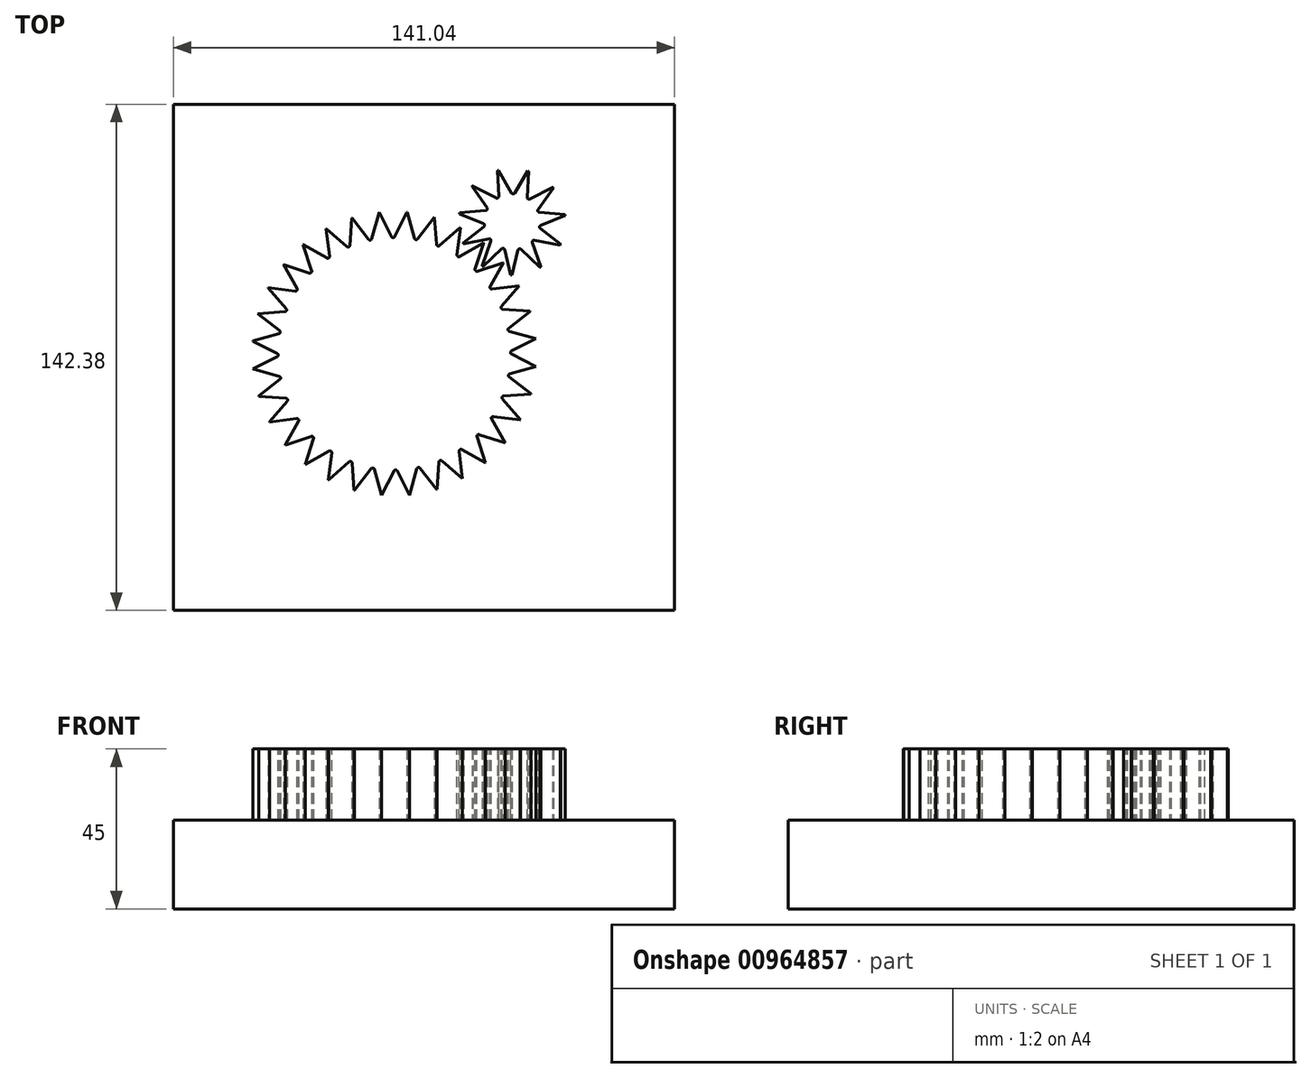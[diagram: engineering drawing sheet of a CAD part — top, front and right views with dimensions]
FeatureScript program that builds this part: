
annotation { "Feature Type Name" : "Feature", "Feature Type Description" : "" }
export const myFeature = defineFeature(function(context is Context, id is Id, definition is map)
    precondition{}
    {
        {
            var Q0;
            Q0=qCreatedBy(makeId("Top.planeOp"),FACE);
            var sketch = newSketch(context, id + "F0", { "sketchPlane" : qUnion([Q0])});
            skCircle(sketch, "E0", {"center": v(0, 0) * mm, "radius": 40 * mm});
            skPoint(sketch, "E1.right.start.orphan", {"position": v(-10, 5) * mm});
            skPoint(sketch, "E1.top.end.orphan", {"position": v(-10, -5) * mm});
            skPoint(sketch, "E1.left.end.orphan", {"position": v(10, -5) * mm});
            skPoint(sketch, "E1.left.start.orphan", {"position": v(10, 5) * mm});
            skSolve(sketch);
        }
        {
            var Q0;
            Q0=makeQuery(id+"F0.imprint","IMPRINT",FACE,{"disambiguationData":[TD([[makeQuery(id+"F0.imprint","IMPRINT",EDGE,{"derivedFrom":sQuery(id+"F0.wireOp",EDGE,"E0")}),1.0]])]});
            extrude(context, id + "F1", {"entities" : qUnion([Q0]), "depth" : 20 * mm, "offsetDistance" : 25 * mm});
        }
        {
            var Q0;
            Q0=makeQuery(id+"F1.opExtrude","CAP_FACE",FACE,{"disambiguationData":[OSD([sQuery(id+"F0.wireOp",EDGE,"E0"),sQuery(id+"F0.wireOp",EDGE,"E1.bottom"),sQuery(id+"F0.wireOp",EDGE,"E1.top"),sQuery(id+"F0.wireOp",EDGE,"E1.left"),sQuery(id+"F0.wireOp",EDGE,"E1.right")])],"isStart":false});
            var sketch = newSketch(context, id + "F2", { "sketchPlane" : qUnion([Q0])});
            skLineSegment(sketch, "E2", {"start": v(-4.86, 41) * mm, "end": v(4.14, 41) * mm});
            skLineSegment(sketch, "E3", {"start": v(4.14, 41) * mm, "end": v(0.08, 32.96) * mm});
            skLineSegment(sketch, "E4", {"start": v(-0.8, 32.96) * mm, "end": v(-4.86, 41) * mm});
            skPoint(sketch, "E5.visualSharp", {"position": v(-0.36, 32.08) * mm});
            skArc(sketch, "E5.filletArc", {"start": v(-0.8, 32.96) * mm, "mid": v(-0.36, 32.69) * mm, "end": v(0.08, 32.96) * mm});
            skSolve(sketch);
        }
        {
            var Q0;
            {var subQ0=sQuery(id+"F2.wireOp",EDGE,"E4");var subQ1=sQuery(id+"F2.wireOp",EDGE,"E3");var subQ2=makeQuery(id+"F2.imprint","INTERSECT",VERTEX,{"derivedFrom":[subQ1,subQ0]});Q0=makeQuery(id+"F2.imprint","IMPRINT",FACE,{"disambiguationData":[TD([[makeQuery(id+"F2.imprint","IMPRINT",EDGE,{"disambiguationData":[TD([[subQ2,1.0]])],"derivedFrom":subQ1}),-1.0]])]});}
            extrude(context, id + "F3", {"entities" : qUnion([Q0]), "operationType" : NewBodyOperationType.REMOVE, "oppositeDirection" : true, "depth" : 25 * mm, "offsetDistance" : 25 * mm});
        }
        {
            var Q0;
            Q0=makeQuery(id+"F3.boolean.opBoolean","COPY",FACE,{"derivedFrom":makeQuery(id+"F3.opExtrude","SWEPT_FACE",FACE,{"disambiguationData":[OSD([sQuery(id+"F2.wireOp",EDGE,"E4")])]})});
            var Q1;
            Q1=makeQuery(id+"F3.boolean.opBoolean","COPY",FACE,{"derivedFrom":makeQuery(id+"F3.opExtrude","SWEPT_FACE",FACE,{"disambiguationData":[OSD([sQuery(id+"F2.wireOp",EDGE,"E3")])]})});
            var Q2;
            Q2=makeQuery(id+"F3.boolean.opBoolean","COPY",FACE,{"derivedFrom":makeQuery(id+"F3.opExtrude","SWEPT_FACE",FACE,{"disambiguationData":[OSD([sQuery(id+"F2.wireOp",EDGE,"E5.filletArc")])]})});
            var Q3;
            Q3=makeQuery(id+"F1.opExtrude","SWEPT_FACE",FACE,{"disambiguationData":[OSD([sQuery(id+"F0.wireOp",EDGE,"E0")])]});
            circularPattern(context, id + "F4", {"patternType" : PatternType.FACE, "faces" : qUnion([Q0, Q1, Q2]), "axis" : qUnion([Q3]), "angle" : 360 * degree, "instanceCount" : 64, "equalSpace" : true});
        }
        {
            var Q0;
            Q0=qCreatedBy(makeId("Top.planeOp"),FACE);
            var sketch = newSketch(context, id + "F5", { "sketchPlane" : qUnion([Q0])});
            skCircle(sketch, "E6", {"center": v(40.75, 48.43) * mm, "radius": 15 * mm});
            skPoint(sketch, "E7.right.end.orphan", {"position": v(38.25, 47.43) * mm});
            skPoint(sketch, "E7.bottom.end.orphan", {"position": v(38.25, 49.43) * mm});
            skPoint(sketch, "E7.left.end.orphan", {"position": v(43.25, 47.43) * mm});
            skPoint(sketch, "E7.left.start.orphan", {"position": v(43.25, 49.43) * mm});
            skSolve(sketch);
        }
        {
            var Q0;
            Q0=makeQuery(id+"F5.imprint","IMPRINT",FACE,{"disambiguationData":[TD([[makeQuery(id+"F5.imprint","IMPRINT",EDGE,{"derivedFrom":sQuery(id+"F5.wireOp",EDGE,"E6")}),1.0]])]});
            extrude(context, id + "F6", {"entities" : qUnion([Q0]), "operationType" : NewBodyOperationType.ADD, "depth" : 20 * mm, "offsetDistance" : 25 * mm});
        }
        {
            var Q0;
            Q0=makeQuery(id+"F6.opExtrude","CAP_FACE",FACE,{"disambiguationData":[OSD([sQuery(id+"F5.wireOp",EDGE,"E6"),sQuery(id+"F5.wireOp",EDGE,"E7.bottom"),sQuery(id+"F5.wireOp",EDGE,"E7.top"),sQuery(id+"F5.wireOp",EDGE,"E7.left"),sQuery(id+"F5.wireOp",EDGE,"E7.right")])],"isStart":false});
            var sketch = newSketch(context, id + "F7", { "sketchPlane" : qUnion([Q0])});
            skLineSegment(sketch, "E8", {"start": v(36.02, 64.43) * mm, "end": v(46.02, 64.43) * mm});
            skLineSegment(sketch, "E9", {"start": v(46.02, 64.43) * mm, "end": v(41.45, 56.52) * mm});
            skLineSegment(sketch, "E10", {"start": v(40.59, 56.52) * mm, "end": v(36.02, 64.43) * mm});
            skPoint(sketch, "E11.visualSharp", {"position": v(41.02, 55.77) * mm});
            skArc(sketch, "E11.filletArc", {"start": v(40.59, 56.52) * mm, "mid": v(41.02, 56.27) * mm, "end": v(41.45, 56.52) * mm});
            skSolve(sketch);
        }
        {
            var Q0;
            {var subQ0=sQuery(id+"F7.wireOp",EDGE,"E10");var subQ1=sQuery(id+"F7.wireOp",EDGE,"E9");var subQ2=makeQuery(id+"F7.imprint","INTERSECT",VERTEX,{"derivedFrom":[subQ1,subQ0]});Q0=makeQuery(id+"F7.imprint","IMPRINT",FACE,{"disambiguationData":[TD([[makeQuery(id+"F7.imprint","IMPRINT",EDGE,{"disambiguationData":[TD([[subQ2,1.0]])],"derivedFrom":subQ1}),-1.0]])]});}
            extrude(context, id + "F8", {"entities" : qUnion([Q0]), "operationType" : NewBodyOperationType.REMOVE, "oppositeDirection" : true, "depth" : 20 * mm, "offsetDistance" : 25 * mm});
        }
        {
            var Q0;
            Q0=makeQuery(id+"F8.boolean.opBoolean","COPY",FACE,{"derivedFrom":makeQuery(id+"F8.opExtrude","SWEPT_FACE",FACE,{"disambiguationData":[OSD([sQuery(id+"F7.wireOp",EDGE,"E10")])]})});
            var Q1;
            Q1=makeQuery(id+"F8.boolean.opBoolean","COPY",FACE,{"derivedFrom":makeQuery(id+"F8.opExtrude","SWEPT_FACE",FACE,{"disambiguationData":[OSD([sQuery(id+"F7.wireOp",EDGE,"E9")])]})});
            var Q2;
            Q2=makeQuery(id+"F8.boolean.opBoolean","COPY",FACE,{"derivedFrom":makeQuery(id+"F8.opExtrude","SWEPT_FACE",FACE,{"disambiguationData":[OSD([sQuery(id+"F7.wireOp",EDGE,"E11.filletArc")])]})});
            var Q3;
            Q3=makeQuery(id+"F6.opExtrude","SWEPT_FACE",FACE,{"disambiguationData":[OSD([sQuery(id+"F5.wireOp",EDGE,"E6")])]});
            circularPattern(context, id + "F9", {"patternType" : PatternType.FACE, "faces" : qUnion([Q0, Q1, Q2]), "axis" : qUnion([Q3]), "angle" : 360 * degree, "instanceCount" : 22, "equalSpace" : true});
        }
        {
            var Q0;
            Q0=qCreatedBy(makeId("Top.planeOp"),FACE);
            var sketch = newSketch(context, id + "F10", { "sketchPlane" : qUnion([Q0])});
            skLineSegment(sketch, "E12.bottom", {"start": v(-62.2, 70.17) * mm, "end": v(78.84, 70.17) * mm});
            skLineSegment(sketch, "E12.top", {"start": v(-62.2, -72.2) * mm, "end": v(78.84, -72.2) * mm});
            skLineSegment(sketch, "E12.left", {"start": v(-62.2, 70.17) * mm, "end": v(-62.2, -72.2) * mm});
            skLineSegment(sketch, "E12.right", {"start": v(78.84, 70.17) * mm, "end": v(78.84, -72.2) * mm});
            skSolve(sketch);
        }
        {
            var Q0;
            Q0=makeQuery(id+"F10.imprint","IMPRINT",FACE,{"disambiguationData":[TD([[makeQuery(id+"F10.imprint","IMPRINT",EDGE,{"derivedFrom":sQuery(id+"F10.wireOp",EDGE,"E12.bottom")}),-1.0]])]});
            extrude(context, id + "F11", {"entities" : qUnion([Q0]), "oppositeDirection" : true, "depth" : 25 * mm, "offsetDistance" : 25 * mm});
        }
        {
            var Q0;
            Q0=makeQuery(id+"F6.opExtrude","SWEPT_BODY",BODY,{"disambiguationData":[OSD([sQuery(id+"F5.wireOp",EDGE,"E6")])]});
            transform(context, id + "F12", {"entities" : qUnion([Q0]), "transformType" : TransformType.TRANSLATION_3D, "dx" : -7.6 * mm, "dy" : -11.3 * mm, "dz" : 0 * mm, "makeCopy" : false});
        }
    });
